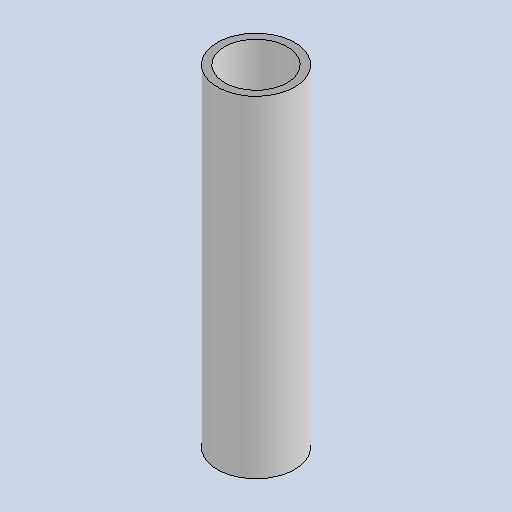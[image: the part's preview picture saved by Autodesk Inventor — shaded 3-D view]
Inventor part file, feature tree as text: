
AUTODESK INVENTOR PART (.ipt)
format: ipt  version: 2025.1 (Build 291241020, 241B)  size: 117,760 bytes
history: native  units: mm
features: extrude x1, sketch x1
ambient origin geometry x8: Origin, YZ Plane, XZ Plane, XY Plane, X Axis, Y Axis, Z Axis, Center Point
bodies: Body1 (feature_tree)
feature tree (2):
  extrude  "Extrusion5"  Depth=90.0mm
  sketch  "Sketch11"  dims[d187=21.0mm d188=2.0mm d189=90.0mm d190=0.0mm]
